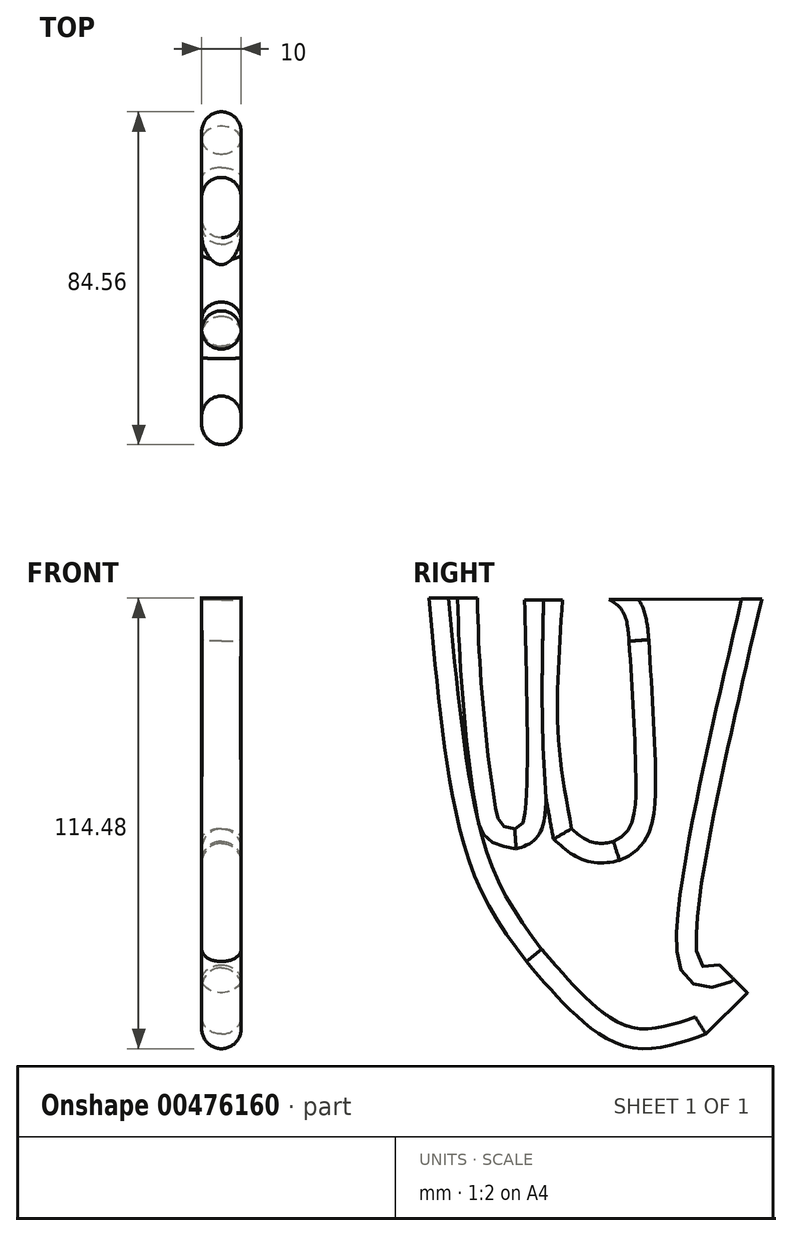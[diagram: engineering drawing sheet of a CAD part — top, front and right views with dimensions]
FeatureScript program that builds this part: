
annotation { "Feature Type Name" : "Feature", "Feature Type Description" : "" }
export const myFeature = defineFeature(function(context is Context, id is Id, definition is map)
    precondition{}
    {
        {
            var Q0;
            Q0=qCreatedBy(makeId("Top.planeOp"),FACE);
            var sketch = newSketch(context, id + "F0", { "sketchPlane" : qUnion([Q0])});
            skLineSegment(sketch, "E0.bottom", {"start": v(50, 50) * mm, "end": v(-50, 50) * mm});
            skLineSegment(sketch, "E0.top", {"start": v(50, -50) * mm, "end": v(-50, -50) * mm});
            skLineSegment(sketch, "E0.left", {"start": v(50, 50) * mm, "end": v(50, -50) * mm});
            skLineSegment(sketch, "E0.right", {"start": v(-50, 50) * mm, "end": v(-50, -50) * mm});
            skPoint(sketch, "E0.middle", {"position": v(0, 0) * mm});
            skSolve(sketch);
        }
        {
            var Q0;
            Q0=qCreatedBy(makeId("Right.planeOp"),FACE);
            var sketch = newSketch(context, id + "F1", { "sketchPlane" : qUnion([Q0])});
            skLineSegment(sketch, "E1", {"start": v(32.93, -92.93) * mm, "end": v(40, -100) * mm});
            skLineSegment(sketch, "E2", {"start": v(40, -100) * mm, "end": v(50, -100) * mm});
            skLineSegment(sketch, "E3", {"start": v(50, -100) * mm, "end": v(50, 0) * mm});
            skLineSegment(sketch, "E4", {"start": v(40, -100) * mm, "end": v(29.49, -110.51) * mm});
            skFitSpline(sketch, "E5", {"points": [v(32.93, -92.93) * mm, v(28.21, -92.93) * mm, v(43.66, 0.05) * mm], "startDerivative": vector(-29.89, -10.4) * mm, "endDerivative": vector(37.17, 160.27) * mm});
            skFitSpline(sketch, "E6", {"points": [v(-40.9, 0.27) * mm, v(-30.42, -67.34) * mm, v(-16.16, -92.08) * mm], "startDerivative": vector(11.48, -125.44) * mm, "endDerivative": vector(40.04, -53.53) * mm});
            skFitSpline(sketch, "E7", {"points": [v(-16.16, -92.08) * mm, v(8.58, -113.48) * mm, v(29.49, -110.51) * mm], "startDerivative": vector(43.98, -51.14) * mm, "endDerivative": vector(47.44, 16.75) * mm});
            skFitSpline(sketch, "E8", {"points": [v(4.84, -0.04) * mm, v(8.45, -3.27) * mm, v(9.97, -10.67) * mm], "startDerivative": vector(9.31, -5.91) * mm, "endDerivative": vector(1.24, -15.02) * mm});
            skFitSpline(sketch, "E9", {"points": [v(9.97, -10.67) * mm, v(11.68, -47.32) * mm, v(9.97, -58.33) * mm, v(5.98, -61.56) * mm], "startDerivative": vector(4.73, -78.25) * mm, "endDerivative": vector(-24.36, -9.02) * mm});
            skFitSpline(sketch, "E10", {"points": [v(5.98, -61.56) * mm, v(-4.65, -58.33) * mm], "startDerivative": vector(-16.52, -4.56) * mm, "endDerivative": vector(-7.97, 6.84) * mm});
            skFitSpline(sketch, "E11", {"points": [v(-4.65, -58.33) * mm, v(-8.07, -34.03) * mm, v(-6.93, -0.23) * mm], "startDerivative": vector(-9.57, 51.96) * mm, "endDerivative": vector(4.67, 65.44) * mm});
            skFitSpline(sketch, "E12", {"points": [v(-16.61, -0.23) * mm, v(-16.61, -55.48) * mm, v(-19.08, -58.33) * mm], "startDerivative": vector(2.52, -90.62) * mm, "endDerivative": vector(-24.76, -8.25) * mm});
            skFitSpline(sketch, "E13", {"points": [v(-19.08, -58.33) * mm, v(-23.45, -55.48) * mm, v(-28.58, 0.27) * mm], "startDerivative": vector(-46.85, 8.92) * mm, "endDerivative": vector(-1.42, 97.49) * mm});
            skLineSegment(sketch, "E14", {"start": v(-28.58, 0.27) * mm, "end": v(-40.9, 0.27) * mm});
            skLineSegment(sketch, "E15", {"start": v(43.66, 0.05) * mm, "end": v(4.84, -0.04) * mm});
            skLineSegment(sketch, "E16", {"start": v(-6.93, -0.23) * mm, "end": v(-16.61, -0.23) * mm});
            skSolve(sketch);
        }
        {
            var Q0;
            Q0=makeQuery(id+"F1.imprint","IMPRINT",FACE,{"disambiguationData":[TD([[makeQuery(id+"F1.imprint","IMPRINT",EDGE,{"derivedFrom":sQuery(id+"F1.wireOp",EDGE,"E1")}),-1.0]])]});
            extrude(context, id + "F2", {"entities" : qUnion([Q0]), "endBound" : BoundingType.SYMMETRIC, "depth" : 10 * mm});
        }
        {
            var Q0;
            Q0=makeQuery(id+"F2.opExtrude","CAP_EDGE",EDGE,{"disambiguationData":[OSD([sQuery(id+"F1.wireOp",EDGE,"E5")])],"isStart":false});
            var Q1;
            Q1=makeQuery(id+"F2.opExtrude","CAP_EDGE",EDGE,{"disambiguationData":[OSD([sQuery(id+"F1.wireOp",EDGE,"E7")])],"isStart":false});
            var Q2;
            Q2=makeQuery(id+"F2.opExtrude","CAP_EDGE",EDGE,{"disambiguationData":[OSD([sQuery(id+"F1.wireOp",EDGE,"E6")])],"isStart":false});
            var Q3;
            Q3=makeQuery(id+"F2.opExtrude","CAP_EDGE",EDGE,{"disambiguationData":[OSD([sQuery(id+"F1.wireOp",EDGE,"E4")])],"isStart":false});
            var Q4;
            Q4=makeQuery(id+"F2.opExtrude","CAP_EDGE",EDGE,{"disambiguationData":[OSD([sQuery(id+"F1.wireOp",EDGE,"E5")])],"isStart":true});
            var Q5;
            Q5=makeQuery(id+"F2.opExtrude","CAP_EDGE",EDGE,{"disambiguationData":[OSD([sQuery(id+"F1.wireOp",EDGE,"E7")])],"isStart":true});
            var Q6;
            Q6=makeQuery(id+"F2.opExtrude","CAP_EDGE",EDGE,{"disambiguationData":[OSD([sQuery(id+"F1.wireOp",EDGE,"E4")])],"isStart":true});
            var Q7;
            Q7=makeQuery(id+"F2.opExtrude","CAP_EDGE",EDGE,{"disambiguationData":[OSD([sQuery(id+"F1.wireOp",EDGE,"E6")])],"isStart":true});
            var Q8;
            Q8=makeQuery(id+"F2.opExtrude","CAP_EDGE",EDGE,{"disambiguationData":[OSD([sQuery(id+"F1.wireOp",EDGE,"E9")])],"isStart":false});
            var Q9;
            Q9=makeQuery(id+"F2.opExtrude","CAP_EDGE",EDGE,{"disambiguationData":[OSD([sQuery(id+"F1.wireOp",EDGE,"E8")])],"isStart":false});
            var Q10;
            Q10=makeQuery(id+"F2.opExtrude","CAP_EDGE",EDGE,{"disambiguationData":[OSD([sQuery(id+"F1.wireOp",EDGE,"E11")])],"isStart":false});
            var Q11;
            Q11=makeQuery(id+"F2.opExtrude","CAP_EDGE",EDGE,{"disambiguationData":[OSD([sQuery(id+"F1.wireOp",EDGE,"E12")])],"isStart":false});
            var Q12;
            Q12=makeQuery(id+"F2.opExtrude","CAP_EDGE",EDGE,{"disambiguationData":[OSD([sQuery(id+"F1.wireOp",EDGE,"E13")])],"isStart":false});
            var Q13;
            Q13=makeQuery(id+"F2.opExtrude","CAP_EDGE",EDGE,{"disambiguationData":[OSD([sQuery(id+"F1.wireOp",EDGE,"E10")])],"isStart":false});
            var Q14;
            Q14=makeQuery(id+"F2.opExtrude","CAP_EDGE",EDGE,{"disambiguationData":[OSD([sQuery(id+"F1.wireOp",EDGE,"E9")])],"isStart":true});
            var Q15;
            Q15=makeQuery(id+"F2.opExtrude","CAP_EDGE",EDGE,{"disambiguationData":[OSD([sQuery(id+"F1.wireOp",EDGE,"E10")])],"isStart":true});
            var Q16;
            Q16=makeQuery(id+"F2.opExtrude","CAP_EDGE",EDGE,{"disambiguationData":[OSD([sQuery(id+"F1.wireOp",EDGE,"E11")])],"isStart":true});
            var Q17;
            Q17=makeQuery(id+"F2.opExtrude","CAP_EDGE",EDGE,{"disambiguationData":[OSD([sQuery(id+"F1.wireOp",EDGE,"E8")])],"isStart":true});
            var Q18;
            Q18=makeQuery(id+"F2.opExtrude","CAP_EDGE",EDGE,{"disambiguationData":[OSD([sQuery(id+"F1.wireOp",EDGE,"E12")])],"isStart":true});
            var Q19;
            Q19=makeQuery(id+"F2.opExtrude","CAP_EDGE",EDGE,{"disambiguationData":[OSD([sQuery(id+"F1.wireOp",EDGE,"E13")])],"isStart":true});
            fillet(context, id + "F3", {"entities" : qUnion([Q0, Q1, Q2, Q3, Q4, Q5, Q6, Q7, Q8, Q9, Q10, Q11, Q12, Q13, Q14, Q15, Q16, Q17, Q18, Q19]), "radius" : 5 * mm, "tangentPropagation" : true, "allowEdgeOverflow" : false});
        }
    });
